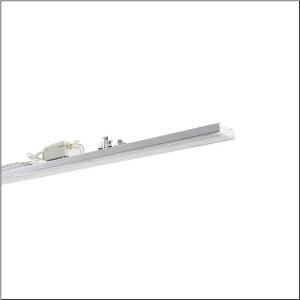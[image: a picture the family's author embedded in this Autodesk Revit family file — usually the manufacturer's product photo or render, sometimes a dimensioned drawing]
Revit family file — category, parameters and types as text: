
# Revit family: licross_r__21_recessed_ho_52te11cn4c5s_4dd9
name_source: partatom
category: Lighting Fixtures
units: mm (PartAtom-declared; Revit-internal decimal feet)

## family parameters
Cut with Voids When Loaded = No
Host = Face
Light Source = No
Part Type = Normal
Room Calculation Point = No
Round Connector Dimension = Use Diameter
Shared = No

## types (1)
- --- (1 x LED, 12640 lm, 68.4 W, 4000K)
    Apparent Load = 68 VA
    CIE Flux Codes = 87 95 99 100 100
    Color Rendering = 80
    Color Temperature = 4000K
    Default Elevation = 1800 mm
    Description = Licross® 21 Recessed HO, luminaire insert, of sheet steel, galvanised, coil coated, white, length: 1.500mm, width: 66mm, height: 67mm, LED rated luminous flux: 12.640lm, light colour: 840, control gear: ON/OFF Multilumen, CLOi, control gear: ECG Multilumen, with plug, 3-pole, with phase selection, mains connection: 220..240V, AC, 50/60Hz, start of lifetime: 68W, end of service life: 83W, halogen-free wiring, primary light control with lens, of plastic, primary optical cover: cover, of PMMA, light emission: direct distribution, primary light characteristic: symmetric, protection rating (complete): IP54, insulation class (complete): insulation class I (protective earthing), certification: CE, ENEC, VDE, UKCA, protection symbol: D if used in an environment with non-conductive dust loads with corresponding accessories, impact resistance: IK06, permissible ambient temperature for indoor applications: -35..+30°C, corresponds to IFS (International Featured Standards) requirements for safety and quality in the food industry, reducing of maximum allowable ambient temperature of 5°C with ceiling mounting, LABS conformity tested according to VDMA 24364:2018-05, packaging unit: 1 piece
    Height = 58 mm
    Lamp = 1 x LED
    Lamp Light Flux = 12640 lm
    Lamp Power = 68.4 W
    Lamp count = 1
    Length = 1500 mm
    Luminous efficacy = 185 lm/W
    Manufacturer = Siteco
    ModVariant = No
    Model = 52TE11CN4C5S
    Mounting Place = Ceiling
    Mounting Type = Pendant
    Number of Poles = 1
    OnlyDefault = Yes
    Power Factor = 1
    Product Name = Licross® 21 Recessed HO
    Product group = luminaire insert
    ProductGroupID = 901
    Protection Class = Protection class I
    Protection Degree = IP 54
    RLX_Detail_Level = 1
    RLX_Emergency_Light_Flux = 0 lm
    RLX_Emergency_Type = 0
    RLX_Emergency_Type_DB = No
    RlxData = <blob elided: 22325 chars, md5=be432c73>
    Socket = socket
    Standby Power = 0 W
    System Light Flux = 12640 lm
    System Power = 68 W
    Type Comments = factory setting: luminous flux: 100 % | (A | C | E) | 161 mA
    Type Image = l_1296930.jpg
    URL = http://relux.com
    VarID = @adj_040785
    Voltage = 0 V
    Weight = 0.00 kg
    Width = 66 mm

## geometry (parser evidence)
native form markers: Blend x4, Sweep x9
no freeform markers — native parametric forms only
